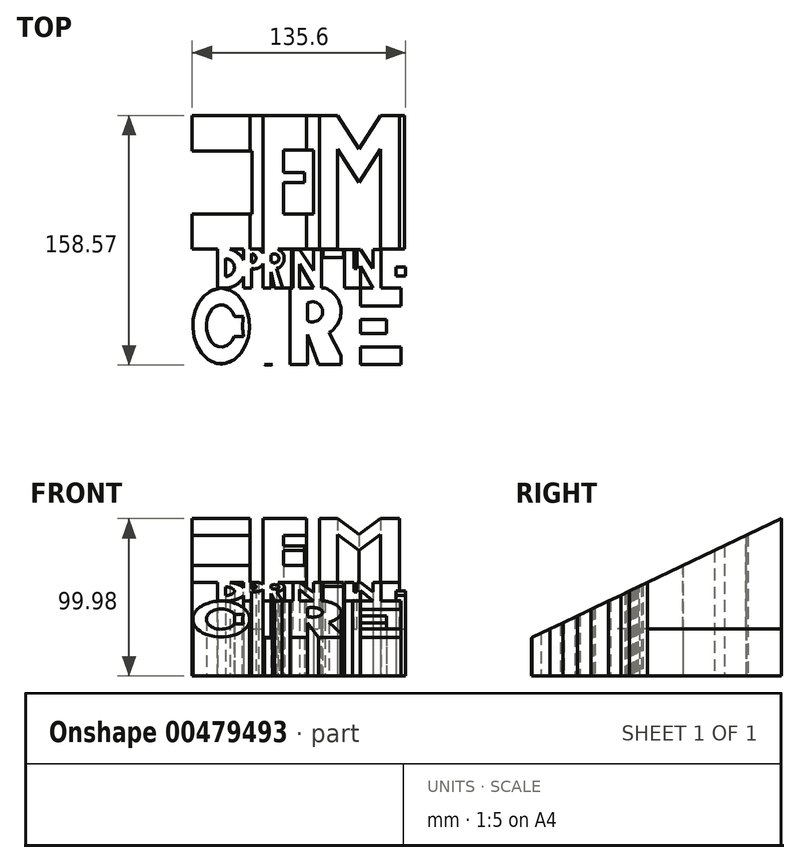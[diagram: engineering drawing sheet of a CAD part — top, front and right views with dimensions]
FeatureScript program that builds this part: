
annotation { "Feature Type Name" : "Feature", "Feature Type Description" : "" }
export const myFeature = defineFeature(function(context is Context, id is Id, definition is map)
    precondition{}
    {
        {
            var Q0;
            Q0=qCreatedBy(makeId("Top.planeOp"),FACE);
            var sketch = newSketch(context, id + "F0", { "sketchPlane" : qUnion([Q0])});
            skLineSegment(sketch, "E0.bottom", {"start": v(-89.26, 70.35) * mm, "end": v(-51.16, 70.35) * mm});
            skLineSegment(sketch, "E0.top", {"start": v(-89.26, 47.87) * mm, "end": v(-51.16, 47.87) * mm});
            skLineSegment(sketch, "E0.left", {"start": v(-89.26, 70.35) * mm, "end": v(-89.26, 47.87) * mm});
            skLineSegment(sketch, "E0.right", {"start": v(-51.16, 70.35) * mm, "end": v(-51.16, 47.87) * mm});
            skLineSegment(sketch, "E1.bottom", {"start": v(-89.26, 7.86) * mm, "end": v(-51.16, 7.86) * mm});
            skLineSegment(sketch, "E1.top", {"start": v(-89.26, -14.63) * mm, "end": v(-51.16, -14.63) * mm});
            skLineSegment(sketch, "E1.left", {"start": v(-89.26, 7.86) * mm, "end": v(-89.26, -14.63) * mm});
            skLineSegment(sketch, "E1.right", {"start": v(-51.16, 7.86) * mm, "end": v(-51.16, -14.63) * mm});
            skLineSegment(sketch, "E2.bottom", {"start": v(-76.85, 47.87) * mm, "end": v(-63.83, 47.87) * mm});
            skLineSegment(sketch, "E2.top", {"start": v(-76.85, 7.86) * mm, "end": v(-63.83, 7.86) * mm});
            skLineSegment(sketch, "E2.left", {"start": v(-76.85, 47.87) * mm, "end": v(-76.85, 7.86) * mm});
            skLineSegment(sketch, "E2.right", {"start": v(-63.83, 47.87) * mm, "end": v(-63.83, 7.86) * mm});
            skLineSegment(sketch, "E3.bottom", {"start": v(-51.16, 70.35) * mm, "end": v(-31.34, 70.35) * mm});
            skLineSegment(sketch, "E3.top", {"start": v(-51.16, -14.63) * mm, "end": v(-31.34, -14.63) * mm});
            skLineSegment(sketch, "E3.left", {"start": v(-51.16, 70.35) * mm, "end": v(-51.16, -14.63) * mm});
            skLineSegment(sketch, "E3.right", {"start": v(-31.34, 70.35) * mm, "end": v(-31.34, -14.63) * mm});
            skLineSegment(sketch, "E4.bottom", {"start": v(-31.34, 70.35) * mm, "end": v(-12.3, 70.35) * mm});
            skLineSegment(sketch, "E4.top", {"start": v(-31.34, 48.25) * mm, "end": v(-12.3, 48.25) * mm});
            skLineSegment(sketch, "E4.left", {"start": v(-31.34, 70.35) * mm, "end": v(-31.34, 48.25) * mm});
            skLineSegment(sketch, "E4.right", {"start": v(-12.3, 70.35) * mm, "end": v(-12.3, 48.25) * mm});
            skLineSegment(sketch, "E5.bottom", {"start": v(-31.34, -14.63) * mm, "end": v(-12.3, -14.63) * mm});
            skLineSegment(sketch, "E5.top", {"start": v(-31.34, 7.86) * mm, "end": v(-12.3, 7.86) * mm});
            skLineSegment(sketch, "E5.left", {"start": v(-31.34, -14.63) * mm, "end": v(-31.34, 7.86) * mm});
            skLineSegment(sketch, "E5.right", {"start": v(-12.3, -14.63) * mm, "end": v(-12.3, 7.86) * mm});
            skLineSegment(sketch, "E6.bottom", {"start": v(-31.34, 27.86) * mm, "end": v(-17.78, 27.86) * mm});
            skLineSegment(sketch, "E6.top", {"start": v(-31.34, 34.13) * mm, "end": v(-17.78, 34.13) * mm});
            skLineSegment(sketch, "E6.left", {"start": v(-31.34, 34.13) * mm, "end": v(-31.34, 27.86) * mm});
            skLineSegment(sketch, "E6.right", {"start": v(-17.78, 34.13) * mm, "end": v(-17.78, 27.86) * mm});
            skLineSegment(sketch, "E7.bottom", {"start": v(-12.3, 70.35) * mm, "end": v(2.95, 70.35) * mm});
            skLineSegment(sketch, "E7.top", {"start": v(-12.3, -14.63) * mm, "end": v(2.95, -14.63) * mm});
            skLineSegment(sketch, "E7.left", {"start": v(-12.3, 70.35) * mm, "end": v(-12.3, -14.63) * mm});
            skLineSegment(sketch, "E7.right", {"start": v(2.95, 70.35) * mm, "end": v(2.95, -14.63) * mm});
            skLineSegment(sketch, "E8.bottom", {"start": v(30.35, 70.35) * mm, "end": v(45.59, 70.35) * mm});
            skLineSegment(sketch, "E8.top", {"start": v(30.35, -14.63) * mm, "end": v(45.59, -14.63) * mm});
            skLineSegment(sketch, "E8.left", {"start": v(30.35, 70.35) * mm, "end": v(30.35, -14.63) * mm});
            skLineSegment(sketch, "E8.right", {"start": v(45.59, 70.35) * mm, "end": v(45.59, -14.63) * mm});
            skLineSegment(sketch, "E9", {"start": v(2.95, 70.35) * mm, "end": v(16.65, 49.1) * mm});
            skLineSegment(sketch, "E10", {"start": v(16.65, 49.1) * mm, "end": v(30.35, 70.35) * mm});
            skLineSegment(sketch, "E11", {"start": v(2.95, 49.1) * mm, "end": v(16.65, 27.86) * mm});
            skPoint(sketch, "E11.endSnap0", {"position": v(2.95, 27.86) * mm});
            skLineSegment(sketch, "E12", {"start": v(16.65, 27.86) * mm, "end": v(30.35, 49.1) * mm});
            skLineSegment(sketch, "E13.bottom", {"start": v(-63.83, 47.87) * mm, "end": v(-51.16, 47.87) * mm});
            skLineSegment(sketch, "E13.top", {"start": v(-63.83, 7.86) * mm, "end": v(-51.16, 7.86) * mm});
            skLineSegment(sketch, "E13.right", {"start": v(-51.16, 47.87) * mm, "end": v(-51.16, 7.86) * mm});
            skSolve(sketch);
        }
        {
            var Q0;
            Q0=qCreatedBy(makeId("Top.planeOp"),FACE);
            var sketch = newSketch(context, id + "F1", { "sketchPlane" : qUnion([Q0])});
            skLineSegment(sketch, "E14.bottom", {"start": v(-73.03, -14.35) * mm, "end": v(-67.95, -14.35) * mm});
            skLineSegment(sketch, "E14.top", {"start": v(-73.03, -39.24) * mm, "end": v(-67.95, -39.24) * mm});
            skLineSegment(sketch, "E14.left", {"start": v(-73.03, -14.35) * mm, "end": v(-73.03, -39.24) * mm});
            skLineSegment(sketch, "E14.right", {"start": v(-67.95, -14.35) * mm, "end": v(-67.95, -39.24) * mm});
            skArc(sketch, "E15", {"start": v(-67.95, -39.24) * mm, "mid": v(-55.5, -26.8) * mm, "end": v(-67.95, -14.35) * mm});
            skArc(sketch, "E16", {"start": v(-67.95, -31.89) * mm, "mid": v(-62.43, -26.25) * mm, "end": v(-67.95, -20.61) * mm});
            skLineSegment(sketch, "E17.bottom", {"start": v(-56.65, -14.35) * mm, "end": v(-51.57, -14.35) * mm});
            skLineSegment(sketch, "E17.top", {"start": v(-56.65, -39.24) * mm, "end": v(-51.57, -39.24) * mm});
            skLineSegment(sketch, "E17.left", {"start": v(-56.65, -14.35) * mm, "end": v(-56.65, -39.24) * mm});
            skLineSegment(sketch, "E17.right", {"start": v(-51.57, -14.35) * mm, "end": v(-51.57, -39.24) * mm});
            skArc(sketch, "E18", {"start": v(-51.57, -26.8) * mm, "mid": v(-43.27, -20.57) * mm, "end": v(-51.57, -14.35) * mm});
            skLineSegment(sketch, "E19", {"start": v(-51.57, -18.35) * mm, "end": v(-51.57, -18.35) * mm});
            skLineSegment(sketch, "E20.bottom", {"start": v(-44.12, -14.35) * mm, "end": v(-39.04, -14.35) * mm});
            skLineSegment(sketch, "E20.top", {"start": v(-44.12, -39.24) * mm, "end": v(-39.04, -39.24) * mm});
            skLineSegment(sketch, "E20.left", {"start": v(-44.12, -14.35) * mm, "end": v(-44.12, -39.24) * mm});
            skLineSegment(sketch, "E20.right", {"start": v(-39.04, -14.35) * mm, "end": v(-39.04, -39.24) * mm});
            skArc(sketch, "E21", {"start": v(-39.04, -26.8) * mm, "mid": v(-30.74, -20.57) * mm, "end": v(-39.04, -14.35) * mm});
            skArc(sketch, "E22", {"start": v(-39.04, -22.42) * mm, "mid": v(-34.12, -20.4) * mm, "end": v(-39.04, -18.4) * mm});
            skLineSegment(sketch, "E23", {"start": v(-31.86, -39.24) * mm, "end": v(-36.94, -39.24) * mm});
            skLineSegment(sketch, "E24", {"start": v(-31.86, -39.24) * mm, "end": v(-35.76, -26.89) * mm});
            skLineSegment(sketch, "E25", {"start": v(-39.04, -29) * mm, "end": v(-36.94, -39.24) * mm});
            skPoint(sketch, "E26.firstSnap0", {"position": v(-30.74, -20.57) * mm});
            skLineSegment(sketch, "E26.right", {"start": v(-26.11, -14.77) * mm, "end": v(-26.11, -39.24) * mm});
            skLineSegment(sketch, "E27.bottom", {"start": v(-26.11, -14.77) * mm, "end": v(-21.03, -14.77) * mm});
            skLineSegment(sketch, "E27.top", {"start": v(-26.11, -39.38) * mm, "end": v(-21.03, -39.38) * mm});
            skLineSegment(sketch, "E27.left", {"start": v(-26.11, -14.77) * mm, "end": v(-26.11, -39.38) * mm});
            skLineSegment(sketch, "E27.right", {"start": v(-21.03, -14.77) * mm, "end": v(-21.03, -39.38) * mm});
            skLineSegment(sketch, "E28", {"start": v(-21.03, -14.77) * mm, "end": v(-12.2, -28.04) * mm});
            skLineSegment(sketch, "E29", {"start": v(-12.2, -28.04) * mm, "end": v(-12.2, -14.77) * mm});
            skLineSegment(sketch, "E30", {"start": v(-21.03, -24.1) * mm, "end": v(-12.2, -39.38) * mm});
            skLineSegment(sketch, "E31", {"start": v(-12.2, -39.38) * mm, "end": v(-7.11, -39.38) * mm});
            skLineSegment(sketch, "E32", {"start": v(-7.11, -39.38) * mm, "end": v(-7.11, -14.77) * mm});
            skLineSegment(sketch, "E33", {"start": v(-7.11, -14.77) * mm, "end": v(-12.2, -14.77) * mm});
            skLineSegment(sketch, "E34.bottom", {"start": v(-7.11, -14.77) * mm, "end": v(7.49, -14.77) * mm});
            skLineSegment(sketch, "E34.top", {"start": v(-7.11, -19.85) * mm, "end": v(7.49, -19.85) * mm});
            skLineSegment(sketch, "E34.left", {"start": v(-7.11, -14.77) * mm, "end": v(-7.11, -19.85) * mm});
            skLineSegment(sketch, "E34.right", {"start": v(7.49, -14.77) * mm, "end": v(7.49, -19.85) * mm});
            skLineSegment(sketch, "E35.bottom", {"start": v(-2.26, -19.85) * mm, "end": v(2.82, -19.85) * mm});
            skLineSegment(sketch, "E35.top", {"start": v(-2.26, -39.24) * mm, "end": v(2.82, -39.24) * mm});
            skLineSegment(sketch, "E35.left", {"start": v(-2.26, -19.85) * mm, "end": v(-2.26, -39.24) * mm});
            skLineSegment(sketch, "E35.right", {"start": v(2.82, -19.85) * mm, "end": v(2.82, -39.24) * mm});
            skPoint(sketch, "E36.firstSnap0", {"position": v(7.49, -16.42) * mm});
            skLineSegment(sketch, "E36.bottom", {"start": v(7.49, -14.77) * mm, "end": v(12.57, -14.77) * mm});
            skLineSegment(sketch, "E36.top", {"start": v(7.49, -39.18) * mm, "end": v(12.57, -39.18) * mm});
            skLineSegment(sketch, "E36.left", {"start": v(7.49, -14.77) * mm, "end": v(7.49, -39.18) * mm});
            skLineSegment(sketch, "E36.right", {"start": v(12.57, -14.77) * mm, "end": v(12.57, -39.18) * mm});
            skLineSegment(sketch, "E37.bottom", {"start": v(12.57, -14.77) * mm, "end": v(17.65, -14.77) * mm});
            skLineSegment(sketch, "E37.top", {"start": v(12.57, -39.38) * mm, "end": v(17.65, -39.38) * mm});
            skLineSegment(sketch, "E37.left", {"start": v(12.57, -14.77) * mm, "end": v(12.57, -39.38) * mm});
            skLineSegment(sketch, "E37.right", {"start": v(17.65, -14.77) * mm, "end": v(17.65, -39.38) * mm});
            skLineSegment(sketch, "E38", {"start": v(17.65, -14.77) * mm, "end": v(25.58, -26.99) * mm});
            skLineSegment(sketch, "E39", {"start": v(25.58, -26.99) * mm, "end": v(25.58, -14.77) * mm});
            skLineSegment(sketch, "E40", {"start": v(17.65, -25.15) * mm, "end": v(25.58, -39.38) * mm});
            skLineSegment(sketch, "E41", {"start": v(25.58, -39.38) * mm, "end": v(30.66, -39.38) * mm});
            skLineSegment(sketch, "E42", {"start": v(30.66, -39.38) * mm, "end": v(30.66, -14.77) * mm});
            skLineSegment(sketch, "E43", {"start": v(30.66, -14.77) * mm, "end": v(25.58, -14.77) * mm});
            skLineSegment(sketch, "E44.bottom", {"start": v(40.35, -25.97) * mm, "end": v(46.34, -25.97) * mm});
            skLineSegment(sketch, "E44.top", {"start": v(40.35, -31.54) * mm, "end": v(46.34, -31.54) * mm});
            skLineSegment(sketch, "E44.left", {"start": v(40.35, -25.97) * mm, "end": v(40.35, -31.54) * mm});
            skLineSegment(sketch, "E44.right", {"start": v(46.34, -25.97) * mm, "end": v(46.34, -31.54) * mm});
            skArc(sketch, "E45", {"start": v(46.3, -22.16) * mm, "mid": v(37.94, -14.8) * mm, "end": v(30.66, -23.22) * mm});
            skArc(sketch, "E46", {"start": v(30.66, -31.54) * mm, "mid": v(38.5, -39.38) * mm, "end": v(46.34, -31.54) * mm});
            skLineSegment(sketch, "E47", {"start": v(46.3, -22.16) * mm, "end": v(40.35, -22.16) * mm});
            skArc(sketch, "E48", {"start": v(40.35, -22.16) * mm, "mid": v(38.47, -20.68) * mm, "end": v(36.6, -22.16) * mm});
            skPoint(sketch, "E49.startSnap0", {"position": v(43.34, -31.54) * mm});
            skLineSegment(sketch, "E50", {"start": v(36.6, -22.16) * mm, "end": v(36.6, -31.68) * mm});
            skArc(sketch, "E51", {"start": v(36.6, -31.68) * mm, "mid": v(40.05, -35.06) * mm, "end": v(43.35, -31.54) * mm});
            skLineSegment(sketch, "E52", {"start": v(30.66, -39.38) * mm, "end": v(38.06, -39.38) * mm});
            skPoint(sketch, "E52.endSnap0", {"position": v(38.5, -39.38) * mm});
            skLineSegment(sketch, "E53", {"start": v(30.66, -14.77) * mm, "end": v(38.47, -14.77) * mm});
            skPoint(sketch, "E53.endSnap0", {"position": v(38.47, -20.68) * mm});
            skArc(sketch, "E54", {"start": v(-51.57, -23.17) * mm, "mid": v(-48.95, -20.31) * mm, "end": v(-51.57, -17.45) * mm});
            skArc(sketch, "E55", {"start": v(-67.95, -31.89) * mm, "mid": v(-62.45, -26.25) * mm, "end": v(-67.95, -20.61) * mm});
            skLineSegment(sketch, "E56", {"start": v(-67.95, -20.61) * mm, "end": v(-67.95, -31.89) * mm});
            skArc(sketch, "E57", {"start": v(-51.57, -23.17) * mm, "mid": v(-48.71, -20.31) * mm, "end": v(-51.57, -17.45) * mm});
            skLineSegment(sketch, "E58", {"start": v(-51.57, -17.45) * mm, "end": v(-51.57, -23.17) * mm});
            skArc(sketch, "E59", {"start": v(-39.04, -22.42) * mm, "mid": v(-34.75, -20.4) * mm, "end": v(-39.04, -18.4) * mm});
            skLineSegment(sketch, "E60", {"start": v(-35.76, -26.89) * mm, "end": v(-31.86, -39.24) * mm});
            skLineSegment(sketch, "E61", {"start": v(-67.95, -39.24) * mm, "end": v(-56.65, -39.24) * mm});
            skLineSegment(sketch, "E62", {"start": v(-51.57, -39.24) * mm, "end": v(-44.12, -39.24) * mm});
            skLineSegment(sketch, "E63", {"start": v(-21.03, -39.38) * mm, "end": v(-12.2, -39.38) * mm});
            skLineSegment(sketch, "E64", {"start": v(2.82, -39.24) * mm, "end": v(7.49, -39.18) * mm});
            skLineSegment(sketch, "E65", {"start": v(17.65, -39.38) * mm, "end": v(25.58, -39.38) * mm});
            skLineSegment(sketch, "E66", {"start": v(-39.04, -39.24) * mm, "end": v(-26.11, -39.24) * mm});
            skLineSegment(sketch, "E67.bottom", {"start": v(-32.23, -14.22) * mm, "end": v(-23.57, -14.22) * mm});
            skLineSegment(sketch, "E67.top", {"start": v(-32.23, -39.38) * mm, "end": v(-23.57, -39.38) * mm});
            skLineSegment(sketch, "E67.left", {"start": v(-32.23, -14.22) * mm, "end": v(-32.23, -39.38) * mm});
            skLineSegment(sketch, "E67.right", {"start": v(-23.57, -14.22) * mm, "end": v(-23.57, -39.38) * mm});
            skSolve(sketch);
        }
        {
            var Q0;
            Q0=qCreatedBy(makeId("Top.planeOp"),FACE);
            var sketch = newSketch(context, id + "F2", { "sketchPlane" : qUnion([Q0])});
            skLineSegment(sketch, "E68", {"start": v(-89.42, -14.56) * mm, "end": v(-81.13, -14.56) * mm});
            skLineSegment(sketch, "E69", {"start": v(-81.13, -14.56) * mm, "end": v(-72.84, -14.56) * mm});
            skArc(sketch, "E70", {"start": v(-72.59, -21.07) * mm, "mid": v(-81.1, -14.56) * mm, "end": v(-89.7, -20.95) * mm});
            skArc(sketch, "E71", {"start": v(-89.98, -30.4) * mm, "mid": v(-81.43, -38.22) * mm, "end": v(-72.38, -30.99) * mm});
            skLineSegment(sketch, "E72", {"start": v(-89.7, -20.95) * mm, "end": v(-86.13, -20.95) * mm});
            skLineSegment(sketch, "E73", {"start": v(-89.98, -30.4) * mm, "end": v(-86.13, -30.4) * mm});
            skLineSegment(sketch, "E74", {"start": v(-81.16, -24.23) * mm, "end": v(-81.16, -27.8) * mm});
            skArc(sketch, "E75", {"start": v(-81.16, -24.23) * mm, "mid": v(-80.8, -18.3) * mm, "end": v(-86.13, -20.95) * mm});
            skArc(sketch, "E76", {"start": v(-86.13, -30.4) * mm, "mid": v(-80.7, -34.74) * mm, "end": v(-81.16, -27.8) * mm});
            skArc(sketch, "E77", {"start": v(-77.53, -26.18) * mm, "mid": v(-74.4, -24.26) * mm, "end": v(-72.59, -21.07) * mm});
            skArc(sketch, "E78", {"start": v(-72.38, -30.99) * mm, "mid": v(-74.34, -27.92) * mm, "end": v(-77.53, -26.18) * mm});
            skPoint(sketch, "E79.endSnap0", {"position": v(-81.43, -38.22) * mm});
            skSolve(sketch);
        }
        {
            var Q0;
            Q0=qCreatedBy(makeId("Top.planeOp"),FACE);
            var sketch = newSketch(context, id + "F3", { "sketchPlane" : qUnion([Q0])});
            skLineSegment(sketch, "E80.bottom", {"start": v(-27.05, -39.34) * mm, "end": v(-16.01, -39.34) * mm});
            skLineSegment(sketch, "E80.top", {"start": v(-27.05, -87.9) * mm, "end": v(-16.01, -87.9) * mm});
            skLineSegment(sketch, "E80.left", {"start": v(-27.05, -39.34) * mm, "end": v(-27.05, -87.9) * mm});
            skLineSegment(sketch, "E80.right", {"start": v(-16.01, -39.34) * mm, "end": v(-16.01, -87.9) * mm});
            skLineSegment(sketch, "E81", {"start": v(-2.07, -87.9) * mm, "end": v(9.8, -87.9) * mm});
            skLineSegment(sketch, "E82.bottom", {"start": v(5.15, -39.34) * mm, "end": v(17.67, -39.34) * mm});
            skLineSegment(sketch, "E82.top", {"start": v(5.15, -87.9) * mm, "end": v(17.67, -87.9) * mm});
            skLineSegment(sketch, "E82.left", {"start": v(5.15, -39.34) * mm, "end": v(5.15, -87.9) * mm});
            skLineSegment(sketch, "E82.right", {"start": v(17.67, -39.34) * mm, "end": v(17.67, -87.9) * mm});
            skLineSegment(sketch, "E83.bottom", {"start": v(17.67, -39.34) * mm, "end": v(43.46, -39.34) * mm});
            skLineSegment(sketch, "E83.top", {"start": v(17.67, -50.64) * mm, "end": v(43.46, -50.64) * mm});
            skLineSegment(sketch, "E83.left", {"start": v(17.67, -39.34) * mm, "end": v(17.67, -50.64) * mm});
            skLineSegment(sketch, "E83.right", {"start": v(43.46, -39.34) * mm, "end": v(43.46, -50.64) * mm});
            skLineSegment(sketch, "E84.bottom", {"start": v(17.67, -87.9) * mm, "end": v(43.46, -87.9) * mm});
            skLineSegment(sketch, "E84.top", {"start": v(17.67, -76.6) * mm, "end": v(43.46, -76.6) * mm});
            skLineSegment(sketch, "E84.left", {"start": v(17.67, -87.9) * mm, "end": v(17.67, -76.6) * mm});
            skLineSegment(sketch, "E84.right", {"start": v(43.46, -87.9) * mm, "end": v(43.46, -76.6) * mm});
            skLineSegment(sketch, "E85.bottom", {"start": v(17.67, -59.12) * mm, "end": v(34.28, -59.12) * mm});
            skLineSegment(sketch, "E85.top", {"start": v(17.67, -68.25) * mm, "end": v(34.28, -68.25) * mm});
            skLineSegment(sketch, "E85.left", {"start": v(17.67, -59.12) * mm, "end": v(17.67, -68.25) * mm});
            skLineSegment(sketch, "E85.right", {"start": v(34.28, -59.12) * mm, "end": v(34.28, -68.25) * mm});
            skPoint(sketch, "E86.endSnap0", {"position": v(-72.4, -92.39) * mm});
            skLineSegment(sketch, "E87", {"start": v(-48.63, -87.9) * mm, "end": v(-27.05, -87.9) * mm});
            skLineSegment(sketch, "E88", {"start": v(-2.07, -87.9) * mm, "end": v(43.46, -87.9) * mm});
            skLineSegment(sketch, "E89", {"start": v(-16.01, -39.34) * mm, "end": v(29.75, -39.34) * mm});
            skLineSegment(sketch, "E90", {"start": v(-27.05, -39.34) * mm, "end": v(-14.53, -39.34) * mm});
            skLineSegment(sketch, "E91", {"start": v(-16.01, -87.9) * mm, "end": v(-2.07, -87.9) * mm});
            skLineSegment(sketch, "E92", {"start": v(-72.57, -87.9) * mm, "end": v(-48.63, -87.9) * mm});
            skPoint(sketch, "E93.startSnap0", {"position": v(-61.69, -59.33) * mm});
            skLineSegment(sketch, "E94", {"start": v(-16.01, -68.75) * mm, "end": v(-9.04, -87.9) * mm});
            skArc(sketch, "E95", {"start": v(-16.01, -68.75) * mm, "mid": v(5.37, -54.04) * mm, "end": v(-16.01, -39.34) * mm});
            skArc(sketch, "E96", {"start": v(-16.01, -59.96) * mm, "mid": v(-6.33, -54.38) * mm, "end": v(-16.01, -48.8) * mm});
            skLineSegment(sketch, "E97", {"start": v(-2.39, -67.61) * mm, "end": v(8.1, -87.9) * mm});
            skEllipse(sketch, "E98", {"center": v(-40.83, -63.37) * mm, "majorRadius": 24.85 * mm, "minorRadius": 16.36 * mm, "majorAxis": v(0, 1)});
            skEllipse(sketch, "E99", {"center": v(-40.83, -63.37) * mm, "majorRadius": 11.51 * mm, "minorRadius": 6.34 * mm, "majorAxis": v(0, 1)});
            skEllipse(sketch, "E100", {"center": v(-70.8, -63.37) * mm, "majorRadius": 24 * mm, "minorRadius": 18.03 * mm, "majorAxis": v(0, 1)});
            skEllipse(sketch, "E101", {"center": v(-70.8, -63.37) * mm, "majorRadius": 13.42 * mm, "minorRadius": 9.43 * mm, "majorAxis": v(0, 1)});
            skLineSegment(sketch, "E102", {"start": v(-62.36, -57.4) * mm, "end": v(-53.34, -57.4) * mm});
            skLineSegment(sketch, "E103", {"start": v(-62.59, -69.96) * mm, "end": v(-53.47, -69.96) * mm});
            skSolve(sketch);
        }
        {
            var Q0;
            Q0=makeQuery(id+"F3.imprint","IMPRINT",FACE,{"disambiguationData":[TD([[makeQuery(id+"F3.imprint","IMPRINT",EDGE,{"derivedFrom":sQuery(id+"F3.wireOp",EDGE,"E93")}),-1.0]])]});
            var Q1;
            {var subQ0=sQuery(id+"F3.wireOp",EDGE,"GElmIXpN-kcJR-45oa-h3sK-QHrJCuWuAJcQ");var subQ1=sQuery(id+"F3.wireOp",EDGE,"etVh0nDV-C5XI-KxPU-PWaB-zNqrgVtYXJuy");var subQ3=makeQuery(id+"F3.imprint","INTERSECT",VERTEX,{"derivedFrom":[subQ1,subQ0]});Q1=makeQuery(id+"F3.imprint","IMPRINT",FACE,{"disambiguationData":[TD([[makeQuery(id+"F3.imprint","IMPRINT",EDGE,{"disambiguationData":[TD([[subQ3,-1.0]])],"derivedFrom":subQ1}),1.0]])]});}
            var Q2;
            Q2=makeQuery(id+"F3.imprint","IMPRINT",FACE,{"disambiguationData":[TD([[makeQuery(id+"F3.imprint","IMPRINT",EDGE,{"derivedFrom":sQuery(id+"F3.wireOp",EDGE,"l2BAxcx8-wpF1-YFFp-7Sex-uG9L4fK84GIy")}),1.0]])]});
            var Q3;
            Q3=makeQuery(id+"F3.imprint","IMPRINT",FACE,{"disambiguationData":[TD([[makeQuery(id+"F3.imprint","IMPRINT",EDGE,{"derivedFrom":sQuery(id+"F3.wireOp",EDGE,"Tai5gYko-rnaj-8Qc9-2tER-s00ccv3sg9T1")}),-1.0]])]});
            var Q4;
            {var subQ0=sQuery(id+"F3.wireOp",EDGE,"etVh0nDV-C5XI-KxPU-PWaB-zNqrgVtYXJuy");var subQ1=sQuery(id+"F3.wireOp",EDGE,"E80.left");var subQ3=makeQuery(id+"F3.imprint","INTERSECT",VERTEX,{"derivedFrom":[subQ1,subQ0]});Q4=makeQuery(id+"F3.imprint","IMPRINT",FACE,{"disambiguationData":[TD([[makeQuery(id+"F3.imprint","IMPRINT",EDGE,{"disambiguationData":[TD([[subQ3,-1.0]])],"derivedFrom":subQ1}),1.0]])]});}
            var Q5;
            {var subQ7=sQuery(id+"F3.wireOp",EDGE,"E80.bottom");Q5=makeQuery(id+"F3.imprint","IMPRINT",FACE,{"disambiguationData":[TD([[makeQuery(id+"F3.imprint","IMPRINT",EDGE,{"derivedFrom":subQ7}),-1.0]])]});}
            var Q6;
            {var subQ0=sQuery(id+"F3.wireOp",EDGE,"9Uwg85qv-AG06-xsUL-vuyy-mQr5ySh0xjGx");var subQ1=sQuery(id+"F3.wireOp",EDGE,"E87");var subQ3=makeQuery(id+"F3.imprint","INTERSECT",VERTEX,{"derivedFrom":[subQ1,subQ0]});Q6=makeQuery(id+"F3.imprint","IMPRINT",FACE,{"disambiguationData":[TD([[makeQuery(id+"F3.imprint","IMPRINT",EDGE,{"disambiguationData":[TD([[subQ3,1.0]])],"derivedFrom":subQ1}),-1.0]])]});}
            var Q7;
            {var subQ0=sQuery(id+"F3.wireOp",EDGE,"9Uwg85qv-AG06-xsUL-vuyy-mQr5ySh0xjGx");var subQ1=sQuery(id+"F3.wireOp",EDGE,"E80.left");var subQ3=makeQuery(id+"F3.imprint","INTERSECT",VERTEX,{"derivedFrom":[subQ1,subQ0]});Q7=makeQuery(id+"F3.imprint","IMPRINT",FACE,{"disambiguationData":[TD([[makeQuery(id+"F3.imprint","IMPRINT",EDGE,{"disambiguationData":[TD([[subQ3,1.0]])],"derivedFrom":subQ1}),1.0]])]});}
            var Q8;
            {var subQ0=sQuery(id+"F3.wireOp",EDGE,"goEZywdV-8XkG-8Sym-g4On-3OGV7yo023wS");var subQ1=sQuery(id+"F3.wireOp",EDGE,"9Uwg85qv-AG06-xsUL-vuyy-mQr5ySh0xjGx");var subQ3=makeQuery(id+"F3.imprint","INTERSECT",VERTEX,{"derivedFrom":[subQ1,subQ0]});Q8=makeQuery(id+"F3.imprint","IMPRINT",FACE,{"disambiguationData":[TD([[makeQuery(id+"F3.imprint","IMPRINT",EDGE,{"disambiguationData":[TD([[subQ3,1.0]])],"derivedFrom":subQ1}),1.0]])]});}
            var Q9;
            {var subQ10=sQuery(id+"F3.wireOp",EDGE,"vgvU5bvX-y910-j5x7-Pnl7-edi9nkagyyvk");Q9=makeQuery(id+"F3.imprint","IMPRINT",FACE,{"disambiguationData":[TD([[makeQuery(id+"F3.imprint","IMPRINT",EDGE,{"derivedFrom":subQ10}),1.0]])]});}
            var Q10;
            {var subQ9=sQuery(id+"F3.wireOp",EDGE,"ZULs1xFT-bYxo-X5Mw-NcRk-gdkzuhtu9iQL");Q10=makeQuery(id+"F3.imprint","IMPRINT",FACE,{"disambiguationData":[TD([[makeQuery(id+"F3.imprint","IMPRINT",EDGE,{"derivedFrom":subQ9}),-1.0]])]});}
            var Q11;
            {var subQ0=sQuery(id+"F3.wireOp",EDGE,"UGmMbKpx-ic0C-BP45-GIFm-G44WuJZ7rcJZ");var subQ1=sQuery(id+"F3.wireOp",EDGE,"E82.left");var subQ2=makeQuery(id+"F3.imprint","INTERSECT",VERTEX,{"disambiguationData":[OD(0.0)],"derivedFrom":[subQ1,subQ0]});Q11=makeQuery(id+"F3.imprint","IMPRINT",FACE,{"disambiguationData":[TD([[makeQuery(id+"F3.imprint","IMPRINT",EDGE,{"disambiguationData":[TD([[subQ2,-1.0]])],"derivedFrom":subQ1}),1.0]])]});}
            var Q12;
            {var subQ5=sQuery(id+"F3.wireOp",EDGE,"5uwGIrsL-Ax3l-KrJ3-TsMS-mPTyOWhAeuEh");Q12=makeQuery(id+"F3.imprint","IMPRINT",FACE,{"disambiguationData":[TD([[makeQuery(id+"F3.imprint","IMPRINT",EDGE,{"derivedFrom":subQ5}),1.0]])]});}
            var Q13;
            {var subQ0=sQuery(id+"F3.wireOp",EDGE,"E88");var subQ1=sQuery(id+"F3.wireOp",EDGE,"QoJ9POKL-7dSj-Kbwg-M42Z-KDTpscI53ORy");var subQ2=makeQuery(id+"F3.imprint","INTERSECT",VERTEX,{"derivedFrom":[subQ1,subQ0]});Q13=makeQuery(id+"F3.imprint","IMPRINT",FACE,{"disambiguationData":[TD([[makeQuery(id+"F3.imprint","IMPRINT",EDGE,{"disambiguationData":[TD([[subQ2,1.0]])],"derivedFrom":subQ1}),-1.0]])]});}
            var Q14;
            {var subQ3=sQuery(id+"F3.wireOp",EDGE,"E83.left");Q14=makeQuery(id+"F3.imprint","IMPRINT",FACE,{"disambiguationData":[TD([[makeQuery(id+"F3.imprint","IMPRINT",EDGE,{"derivedFrom":subQ3}),-1.0]])]});}
            var Q15;
            Q15=makeQuery(id+"F3.imprint","IMPRINT",FACE,{"disambiguationData":[TD([[makeQuery(id+"F3.imprint","IMPRINT",EDGE,{"derivedFrom":sQuery(id+"F3.wireOp",EDGE,"E84.top")}),-1.0]])]});
            var Q16;
            Q16=makeQuery(id+"F3.imprint","IMPRINT",FACE,{"disambiguationData":[TD([[makeQuery(id+"F3.imprint","IMPRINT",EDGE,{"derivedFrom":sQuery(id+"F3.wireOp",EDGE,"E85.bottom")}),-1.0]])]});
            var Q17;
            {var subQ1=sQuery(id+"F3.wireOp",EDGE,"E83.bottom");Q17=makeQuery(id+"F3.imprint","IMPRINT",FACE,{"disambiguationData":[TD([[makeQuery(id+"F3.imprint","IMPRINT",EDGE,{"derivedFrom":subQ1}),-1.0]])]});}
            var Q18;
            {var subQ5=sQuery(id+"F3.wireOp",EDGE,"E80.top");Q18=makeQuery(id+"F3.imprint","IMPRINT",FACE,{"disambiguationData":[TD([[makeQuery(id+"F3.imprint","IMPRINT",EDGE,{"derivedFrom":subQ5}),1.0]])]});}
            var Q19;
            {var subQ0=sQuery(id+"F3.wireOp",EDGE,"iaVYXmuH-C6zT-0Hll-rQQs-5zNDWjSzhZfG");var subQ1=sQuery(id+"F3.wireOp",EDGE,"E82.left");var subQ2=makeQuery(id+"F3.imprint","INTERSECT",VERTEX,{"disambiguationData":[OD(0.0)],"derivedFrom":[subQ1,subQ0]});Q19=makeQuery(id+"F3.imprint","IMPRINT",FACE,{"disambiguationData":[TD([[makeQuery(id+"F3.imprint","IMPRINT",EDGE,{"disambiguationData":[TD([[subQ2,-1.0]])],"derivedFrom":subQ1}),1.0]])]});}
            var Q20;
            {var subQ10=sQuery(id+"F3.wireOp",EDGE,"W87mtJ7x-wgiw-5JIF-yIz9-pi0v8XZ7OW02");Q20=makeQuery(id+"F3.imprint","IMPRINT",FACE,{"disambiguationData":[TD([[makeQuery(id+"F3.imprint","IMPRINT",EDGE,{"derivedFrom":subQ10}),-1.0]])]});}
            var Q21;
            {var subQ0=sQuery(id+"F3.wireOp",EDGE,"L14g0OWl-b5Mz-6KAP-ZlKC-kIkRNDyMzksr");var subQ1=sQuery(id+"F3.wireOp",EDGE,"E82.left");var subQ2=makeQuery(id+"F3.imprint","INTERSECT",VERTEX,{"disambiguationData":[OD(0.0)],"derivedFrom":[subQ1,subQ0]});Q21=makeQuery(id+"F3.imprint","IMPRINT",FACE,{"disambiguationData":[TD([[makeQuery(id+"F3.imprint","IMPRINT",EDGE,{"disambiguationData":[TD([[subQ2,-1.0]])],"derivedFrom":subQ1}),1.0]])]});}
            var Q22;
            {var subQ3=sQuery(id+"F3.wireOp",EDGE,"E96");Q22=makeQuery(id+"F3.imprint","IMPRINT",FACE,{"disambiguationData":[TD([[makeQuery(id+"F3.imprint","IMPRINT",EDGE,{"derivedFrom":subQ3}),-1.0]])]});}
            var Q23;
            {var subQ0=sQuery(id+"F3.wireOp",EDGE,"E94");Q23=makeQuery(id+"F3.imprint","IMPRINT",FACE,{"disambiguationData":[TD([[makeQuery(id+"F3.imprint","IMPRINT",EDGE,{"derivedFrom":subQ0}),1.0]])]});}
            var Q24;
            {var subQ0=sQuery(id+"F3.wireOp",EDGE,"E95");var subQ1=sQuery(id+"F3.wireOp",EDGE,"E82.left");var subQ2=makeQuery(id+"F3.imprint","INTERSECT",VERTEX,{"disambiguationData":[OD(0.0)],"derivedFrom":[subQ1,subQ0]});Q24=makeQuery(id+"F3.imprint","IMPRINT",FACE,{"disambiguationData":[TD([[makeQuery(id+"F3.imprint","IMPRINT",EDGE,{"disambiguationData":[TD([[subQ2,-1.0]])],"derivedFrom":subQ1}),1.0]])]});}
            var Q25;
            {var subQ0=sQuery(id+"F3.wireOp",EDGE,"E88");var subQ1=sQuery(id+"F3.wireOp",EDGE,"E82.left");var subQ2=makeQuery(id+"F3.imprint","INTERSECT",VERTEX,{"derivedFrom":[subQ1,subQ0]});Q25=makeQuery(id+"F3.imprint","IMPRINT",FACE,{"disambiguationData":[TD([[makeQuery(id+"F3.imprint","IMPRINT",EDGE,{"disambiguationData":[TD([[subQ2,1.0]])],"derivedFrom":subQ1}),1.0]])]});}
            var Q26;
            {var subQ0=sQuery(id+"F3.wireOp",EDGE,"dAoB9NSq-ERkH-hq60-yBYx-hBlx5KMwvAX0");Q26=makeQuery(id+"F3.imprint","IMPRINT",FACE,{"disambiguationData":[TD([[makeQuery(id+"F3.imprint","IMPRINT",EDGE,{"derivedFrom":subQ0}),-1.0]])]});}
            var Q27;
            Q27=makeQuery(id+"F3.imprint","IMPRINT",FACE,{"disambiguationData":[TD([[makeQuery(id+"F3.imprint","IMPRINT",EDGE,{"derivedFrom":sQuery(id+"F3.wireOp",EDGE,"E99")}),-1.0]])]});
            var Q28;
            {var subQ0=sQuery(id+"F3.wireOp",EDGE,"FfS5zIeq-Qh4c-nK4M-JezB-Kwh0gAgPYNTQ");var subQ1=sQuery(id+"F3.wireOp",EDGE,"E98");var subQ2=makeQuery(id+"F3.imprint","INTERSECT",VERTEX,{"disambiguationData":[OD(0.0)],"derivedFrom":[subQ1,subQ0]});Q28=makeQuery(id+"F3.imprint","IMPRINT",FACE,{"disambiguationData":[TD([[makeQuery(id+"F3.imprint","IMPRINT",EDGE,{"disambiguationData":[TD([[subQ2,1.0]])],"derivedFrom":subQ1}),1.0]])]});}
            var Q29;
            {var subQ0=sQuery(id+"F3.wireOp",EDGE,"XQu2pely-f4cg-mbWW-zxsq-JVxlkJcybIhI");Q29=makeQuery(id+"F3.imprint","IMPRINT",FACE,{"disambiguationData":[TD([[makeQuery(id+"F3.imprint","IMPRINT",EDGE,{"derivedFrom":subQ0}),1.0]])]});}
            var Q30;
            {var subQ5=sQuery(id+"F3.wireOp",EDGE,"E100");var subQ6=sQuery(id+"F3.wireOp",EDGE,"E98");var subQ10=makeQuery(id+"F3.imprint","INTERSECT",VERTEX,{"disambiguationData":[OD(0.0)],"derivedFrom":[subQ6,subQ5]});Q30=makeQuery(id+"F3.imprint","IMPRINT",FACE,{"disambiguationData":[TD([[makeQuery(id+"F3.imprint","IMPRINT",EDGE,{"disambiguationData":[TD([[subQ10,-1.0]])],"derivedFrom":subQ6}),-1.0]])]});}
            var Q31;
            {var subQ0=sQuery(id+"F3.wireOp",EDGE,"E100");var subQ1=sQuery(id+"F3.wireOp",EDGE,"E98");var subQ2=makeQuery(id+"F3.imprint","INTERSECT",VERTEX,{"disambiguationData":[OD(0.0)],"derivedFrom":[subQ1,subQ0]});Q31=makeQuery(id+"F3.imprint","IMPRINT",FACE,{"disambiguationData":[TD([[makeQuery(id+"F3.imprint","IMPRINT",EDGE,{"disambiguationData":[TD([[subQ2,-1.0]])],"derivedFrom":subQ1}),1.0]])]});}
            var Q32;
            {var subQ0=sQuery(id+"F3.wireOp",EDGE,"E100");var subQ1=sQuery(id+"F3.wireOp",EDGE,"E98");var subQ2=makeQuery(id+"F3.imprint","INTERSECT",VERTEX,{"disambiguationData":[OD(1.0)],"derivedFrom":[subQ1,subQ0]});Q32=makeQuery(id+"F3.imprint","IMPRINT",FACE,{"disambiguationData":[TD([[makeQuery(id+"F3.imprint","IMPRINT",EDGE,{"disambiguationData":[TD([[subQ2,1.0]])],"derivedFrom":subQ1}),1.0]])]});}
            var Q33;
            {var subQ0=sQuery(id+"F3.wireOp",EDGE,"E90");var subQ1=sQuery(id+"F3.wireOp",EDGE,"E89");var subQ2=makeQuery(id+"F3.imprint","INTERSECT",VERTEX,{"derivedFrom":[subQ1,subQ0]});Q33=makeQuery(id+"F3.imprint","IMPRINT",FACE,{"disambiguationData":[TD([[makeQuery(id+"F3.imprint","IMPRINT",EDGE,{"disambiguationData":[TD([[subQ2,-1.0]])],"derivedFrom":subQ1}),1.0]])]});}
            var Q34;
            {var subQ0=sQuery(id+"F3.wireOp",EDGE,"E98");var subQ1=sQuery(id+"F3.wireOp",EDGE,"E80.left");var subQ2=makeQuery(id+"F3.imprint","INTERSECT",VERTEX,{"disambiguationData":[OD(0.0)],"derivedFrom":[subQ1,subQ0]});Q34=makeQuery(id+"F3.imprint","IMPRINT",FACE,{"disambiguationData":[TD([[makeQuery(id+"F3.imprint","IMPRINT",EDGE,{"disambiguationData":[TD([[subQ2,-1.0]])],"derivedFrom":subQ1}),1.0]])]});}
            var Q35;
            {var subQ0=sQuery(id+"F3.wireOp",EDGE,"E102");var subQ1=sQuery(id+"F3.wireOp",EDGE,"E98");var subQ2=makeQuery(id+"F3.imprint","INTERSECT",VERTEX,{"derivedFrom":[subQ1,subQ0]});Q35=makeQuery(id+"F3.imprint","IMPRINT",FACE,{"disambiguationData":[TD([[makeQuery(id+"F3.imprint","IMPRINT",EDGE,{"disambiguationData":[TD([[subQ2,-1.0]])],"derivedFrom":subQ1}),1.0]])]});}
            extrude(context, id + "F4", {"entities" : qUnion([Q0, Q1, Q2, Q3, Q4, Q5, Q6, Q7, Q8, Q9, Q10, Q11, Q12, Q13, Q14, Q15, Q16, Q17, Q18, Q19, Q20, Q21, Q22, Q23, Q24, Q25, Q26, Q27, Q28, Q29, Q30, Q31, Q32, Q33, Q34, Q35]), "depth" : 100 * mm, "offsetDistance" : 25 * mm});
        }
        {
            var Q0;
            Q0=makeQuery(id+"F2.imprint","IMPRINT",FACE,{"disambiguationData":[TD([[makeQuery(id+"F2.imprint","IMPRINT",EDGE,{"derivedFrom":sQuery(id+"F2.wireOp",EDGE,"E71")}),1.0]])]});
            var Q1;
            {var subQ2=sQuery(id+"F1.wireOp",EDGE,"E14.bottom");Q1=makeQuery(id+"F1.imprint","IMPRINT",FACE,{"disambiguationData":[TD([[makeQuery(id+"F1.imprint","IMPRINT",EDGE,{"derivedFrom":subQ2}),-1.0]])]});}
            var Q2;
            {var subQ9=sQuery(id+"F1.wireOp",EDGE,"E16");Q2=makeQuery(id+"F1.imprint","IMPRINT",FACE,{"disambiguationData":[TD([[makeQuery(id+"F1.imprint","IMPRINT",EDGE,{"derivedFrom":subQ9}),-1.0]])]});}
            var Q3;
            {var subQ0=sQuery(id+"F1.wireOp",EDGE,"E17.left");var subQ1=sQuery(id+"F1.wireOp",EDGE,"E15");var subQ2=makeQuery(id+"F1.imprint","INTERSECT",VERTEX,{"disambiguationData":[OD(0.0)],"derivedFrom":[subQ1,subQ0]});Q3=makeQuery(id+"F1.imprint","IMPRINT",FACE,{"disambiguationData":[TD([[makeQuery(id+"F1.imprint","IMPRINT",EDGE,{"disambiguationData":[TD([[subQ2,1.0]])],"derivedFrom":subQ1}),1.0]])]});}
            var Q4;
            {var subQ1=sQuery(id+"F1.wireOp",EDGE,"E17.bottom");Q4=makeQuery(id+"F1.imprint","IMPRINT",FACE,{"disambiguationData":[TD([[makeQuery(id+"F1.imprint","IMPRINT",EDGE,{"derivedFrom":subQ1}),-1.0]])]});}
            var Q5;
            {var subQ6=sQuery(id+"F1.wireOp",EDGE,"E57");Q5=makeQuery(id+"F1.imprint","IMPRINT",FACE,{"disambiguationData":[TD([[makeQuery(id+"F1.imprint","IMPRINT",EDGE,{"derivedFrom":subQ6}),-1.0]])]});}
            var Q6;
            {var subQ0=sQuery(id+"F1.wireOp",EDGE,"E20.left");var subQ1=sQuery(id+"F1.wireOp",EDGE,"E18");var subQ2=makeQuery(id+"F1.imprint","INTERSECT",VERTEX,{"disambiguationData":[OD(0.0)],"derivedFrom":[subQ1,subQ0]});Q6=makeQuery(id+"F1.imprint","IMPRINT",FACE,{"disambiguationData":[TD([[makeQuery(id+"F1.imprint","IMPRINT",EDGE,{"disambiguationData":[TD([[subQ2,1.0]])],"derivedFrom":subQ1}),1.0]])]});}
            var Q7;
            {var subQ1=sQuery(id+"F1.wireOp",EDGE,"E20.bottom");Q7=makeQuery(id+"F1.imprint","IMPRINT",FACE,{"disambiguationData":[TD([[makeQuery(id+"F1.imprint","IMPRINT",EDGE,{"derivedFrom":subQ1}),-1.0]])]});}
            var Q8;
            {var subQ7=sQuery(id+"F1.wireOp",EDGE,"E22");Q8=makeQuery(id+"F1.imprint","IMPRINT",FACE,{"disambiguationData":[TD([[makeQuery(id+"F1.imprint","IMPRINT",EDGE,{"derivedFrom":subQ7}),-1.0]])]});}
            var Q9;
            {var subQ0=sQuery(id+"F1.wireOp",EDGE,"E25");Q9=makeQuery(id+"F1.imprint","IMPRINT",FACE,{"disambiguationData":[TD([[makeQuery(id+"F1.imprint","IMPRINT",EDGE,{"derivedFrom":subQ0}),1.0]])]});}
            var Q10;
            {var subQ0=sQuery(id+"F1.wireOp",EDGE,"iecyQkMB-DT64-ASyu-M7pA-KW5DgSD818Z4.left");var subQ1=sQuery(id+"F1.wireOp",EDGE,"E21");var subQ2=makeQuery(id+"F1.imprint","INTERSECT",VERTEX,{"disambiguationData":[OD(0.0)],"derivedFrom":[subQ1,subQ0]});Q10=makeQuery(id+"F1.imprint","IMPRINT",FACE,{"disambiguationData":[TD([[makeQuery(id+"F1.imprint","IMPRINT",EDGE,{"disambiguationData":[TD([[subQ2,1.0]])],"derivedFrom":subQ1}),1.0]])]});}
            var Q11;
            {var subQ3=sQuery(id+"F1.wireOp",EDGE,"E27.bottom");Q11=makeQuery(id+"F1.imprint","IMPRINT",FACE,{"disambiguationData":[TD([[makeQuery(id+"F1.imprint","IMPRINT",EDGE,{"derivedFrom":subQ3}),-1.0]])]});}
            var Q12;
            {var subQ1=sQuery(id+"F1.wireOp",EDGE,"E28");Q12=makeQuery(id+"F1.imprint","IMPRINT",FACE,{"disambiguationData":[TD([[makeQuery(id+"F1.imprint","IMPRINT",EDGE,{"derivedFrom":subQ1}),-1.0]])]});}
            var Q13;
            {var subQ5=sQuery(id+"F1.wireOp",EDGE,"E34.bottom");Q13=makeQuery(id+"F1.imprint","IMPRINT",FACE,{"disambiguationData":[TD([[makeQuery(id+"F1.imprint","IMPRINT",EDGE,{"derivedFrom":subQ5}),-1.0]])]});}
            var Q14;
            Q14=makeQuery(id+"F1.imprint","IMPRINT",FACE,{"disambiguationData":[TD([[makeQuery(id+"F1.imprint","IMPRINT",EDGE,{"derivedFrom":sQuery(id+"F1.wireOp",EDGE,"E35.bottom")}),-1.0]])]});
            var Q15;
            {var subQ3=sQuery(id+"F1.wireOp",EDGE,"E36.bottom");Q15=makeQuery(id+"F1.imprint","IMPRINT",FACE,{"disambiguationData":[TD([[makeQuery(id+"F1.imprint","IMPRINT",EDGE,{"derivedFrom":subQ3}),-1.0]])]});}
            var Q16;
            {var subQ1=sQuery(id+"F1.wireOp",EDGE,"E37.bottom");Q16=makeQuery(id+"F1.imprint","IMPRINT",FACE,{"disambiguationData":[TD([[makeQuery(id+"F1.imprint","IMPRINT",EDGE,{"derivedFrom":subQ1}),-1.0]])]});}
            var Q17;
            {var subQ1=sQuery(id+"F1.wireOp",EDGE,"E38");Q17=makeQuery(id+"F1.imprint","IMPRINT",FACE,{"disambiguationData":[TD([[makeQuery(id+"F1.imprint","IMPRINT",EDGE,{"derivedFrom":subQ1}),-1.0]])]});}
            var Q18;
            Q18=makeQuery(id+"F1.imprint","IMPRINT",FACE,{"disambiguationData":[TD([[makeQuery(id+"F1.imprint","IMPRINT",EDGE,{"derivedFrom":sQuery(id+"F1.wireOp",EDGE,"E44.bottom")}),-1.0]])]});
            var Q19;
            {var subQ0=sQuery(id+"F1.wireOp",EDGE,"E45");var subQ1=sQuery(id+"F1.wireOp",EDGE,"E42");var subQ2=makeQuery(id+"F1.imprint","INTERSECT",VERTEX,{"disambiguationData":[OD(0.0)],"derivedFrom":[subQ1,subQ0]});Q19=makeQuery(id+"F1.imprint","IMPRINT",FACE,{"disambiguationData":[TD([[makeQuery(id+"F1.imprint","IMPRINT",EDGE,{"disambiguationData":[TD([[subQ2,-1.0]])],"derivedFrom":subQ1}),1.0]])]});}
            var Q20;
            {var subQ3=sQuery(id+"F1.wireOp",EDGE,"E46");Q20=makeQuery(id+"F1.imprint","IMPRINT",FACE,{"disambiguationData":[TD([[makeQuery(id+"F1.imprint","IMPRINT",EDGE,{"derivedFrom":subQ3}),1.0]])]});}
            var Q21;
            {var subQ0=sQuery(id+"F1.wireOp",EDGE,"E67.left");var subQ1=sQuery(id+"F1.wireOp",EDGE,"E21");var subQ2=makeQuery(id+"F1.imprint","INTERSECT",VERTEX,{"disambiguationData":[OD(0.0)],"derivedFrom":[subQ1,subQ0]});Q21=makeQuery(id+"F1.imprint","IMPRINT",FACE,{"disambiguationData":[TD([[makeQuery(id+"F1.imprint","IMPRINT",EDGE,{"disambiguationData":[TD([[subQ2,1.0]])],"derivedFrom":subQ1}),1.0]])]});}
            var Q22;
            {var subQ1=sQuery(id+"F1.wireOp",EDGE,"E27.top");Q22=makeQuery(id+"F1.imprint","IMPRINT",FACE,{"disambiguationData":[TD([[makeQuery(id+"F1.imprint","IMPRINT",EDGE,{"derivedFrom":subQ1}),1.0]])]});}
            var Q23;
            Q23=makeQuery(id+"F4.opExtrude","CAP_FACE",FACE,{"disambiguationData":[OSD([sQuery(id+"F3.wireOp",EDGE,"E80.top"),sQuery(id+"F3.wireOp",EDGE,"E80.left"),sQuery(id+"F3.wireOp",EDGE,"E80.right"),sQuery(id+"F3.wireOp",EDGE,"E82.left"),sQuery(id+"F3.wireOp",EDGE,"E82.right"),sQuery(id+"F3.wireOp",EDGE,"E83.bottom"),sQuery(id+"F3.wireOp",EDGE,"E83.top"),sQuery(id+"F3.wireOp",EDGE,"E83.right"),sQuery(id+"F3.wireOp",EDGE,"E84.top"),sQuery(id+"F3.wireOp",EDGE,"E84.right"),sQuery(id+"F3.wireOp",EDGE,"E85.bottom"),sQuery(id+"F3.wireOp",EDGE,"E85.top"),sQuery(id+"F3.wireOp",EDGE,"E85.right"),sQuery(id+"F3.wireOp",EDGE,"E88"),sQuery(id+"F3.wireOp",EDGE,"E89"),sQuery(id+"F3.wireOp",EDGE,"E90"),sQuery(id+"F3.wireOp",EDGE,"E91"),sQuery(id+"F3.wireOp",EDGE,"E94"),sQuery(id+"F3.wireOp",EDGE,"E95"),sQuery(id+"F3.wireOp",EDGE,"E96"),sQuery(id+"F3.wireOp",EDGE,"E97"),sQuery(id+"F3.wireOp",EDGE,"E98")])],"isStart":false});
            extrude(context, id + "F5", {"entities" : qUnion([Q0, Q1, Q2, Q3, Q4, Q5, Q6, Q7, Q8, Q9, Q10, Q11, Q12, Q13, Q14, Q15, Q16, Q17, Q18, Q19, Q20, Q21, Q22, Q23]), "operationType" : NewBodyOperationType.ADD, "depth" : 100 * mm, "offsetDistance" : 25 * mm});
        }
        {
            var Q0;
            Q0=makeQuery(id+"F0.imprint","IMPRINT",FACE,{"disambiguationData":[TD([[makeQuery(id+"F0.imprint","IMPRINT",EDGE,{"derivedFrom":sQuery(id+"F0.wireOp",EDGE,"E2.bottom")}),-1.0]])]});
            var Q1;
            {var subQ0=sQuery(id+"F0.wireOp",EDGE,"E0.bottom");Q1=makeQuery(id+"F0.imprint","IMPRINT",FACE,{"disambiguationData":[TD([[makeQuery(id+"F0.imprint","IMPRINT",EDGE,{"derivedFrom":subQ0}),-1.0]])]});}
            var Q2;
            Q2=makeQuery(id+"F0.imprint","IMPRINT",FACE,{"disambiguationData":[TD([[makeQuery(id+"F0.imprint","IMPRINT",EDGE,{"derivedFrom":sQuery(id+"F0.wireOp",EDGE,"E1.bottom")}),-1.0]])]});
            var Q3;
            {var subQ4=sQuery(id+"F0.wireOp",EDGE,"E3.bottom");Q3=makeQuery(id+"F0.imprint","IMPRINT",FACE,{"disambiguationData":[TD([[makeQuery(id+"F0.imprint","IMPRINT",EDGE,{"derivedFrom":subQ4}),-1.0]])]});}
            var Q4;
            {var subQ0=sQuery(id+"F0.wireOp",EDGE,"E5.bottom");Q4=makeQuery(id+"F0.imprint","IMPRINT",FACE,{"disambiguationData":[TD([[makeQuery(id+"F0.imprint","IMPRINT",EDGE,{"derivedFrom":subQ0}),1.0]])]});}
            var Q5;
            Q5=makeQuery(id+"F0.imprint","IMPRINT",FACE,{"disambiguationData":[TD([[makeQuery(id+"F0.imprint","IMPRINT",EDGE,{"derivedFrom":sQuery(id+"F0.wireOp",EDGE,"E6.bottom")}),1.0]])]});
            var Q6;
            {var subQ0=sQuery(id+"F0.wireOp",EDGE,"E4.bottom");Q6=makeQuery(id+"F0.imprint","IMPRINT",FACE,{"disambiguationData":[TD([[makeQuery(id+"F0.imprint","IMPRINT",EDGE,{"derivedFrom":subQ0}),-1.0]])]});}
            var Q7;
            {var subQ3=sQuery(id+"F0.wireOp",EDGE,"E7.bottom");Q7=makeQuery(id+"F0.imprint","IMPRINT",FACE,{"disambiguationData":[TD([[makeQuery(id+"F0.imprint","IMPRINT",EDGE,{"derivedFrom":subQ3}),-1.0]])]});}
            var Q8;
            {var subQ1=sQuery(id+"F0.wireOp",EDGE,"E9");Q8=makeQuery(id+"F0.imprint","IMPRINT",FACE,{"disambiguationData":[TD([[makeQuery(id+"F0.imprint","IMPRINT",EDGE,{"derivedFrom":subQ1}),-1.0]])]});}
            var Q9;
            {var subQ3=sQuery(id+"F0.wireOp",EDGE,"E8.bottom");Q9=makeQuery(id+"F0.imprint","IMPRINT",FACE,{"disambiguationData":[TD([[makeQuery(id+"F0.imprint","IMPRINT",EDGE,{"derivedFrom":subQ3}),-1.0]])]});}
            var Q10;
            {var subQ0=sQuery(id+"F1.wireOp",EDGE,"E27.left");Q10=makeQuery(id+"F1.imprint","IMPRINT",FACE,{"disambiguationData":[TD([[makeQuery(id+"F1.imprint","IMPRINT",EDGE,{"derivedFrom":subQ0}),-1.0]])]});}
            var Q11;
            {var subQ0=sQuery(id+"F1.wireOp",EDGE,"E67.left");var subQ1=sQuery(id+"F1.wireOp",EDGE,"E60");var subQ2=makeQuery(id+"F1.imprint","INTERSECT",VERTEX,{"derivedFrom":[subQ1,subQ0]});Q11=makeQuery(id+"F1.imprint","IMPRINT",FACE,{"disambiguationData":[TD([[makeQuery(id+"F1.imprint","IMPRINT",EDGE,{"disambiguationData":[TD([[subQ2,-1.0]])],"derivedFrom":subQ1}),-1.0]])]});}
            var Q12;
            {var subQ14=sQuery(id+"F1.wireOp",EDGE,"E67.bottom");Q12=makeQuery(id+"F1.imprint","IMPRINT",FACE,{"disambiguationData":[TD([[makeQuery(id+"F1.imprint","IMPRINT",EDGE,{"derivedFrom":subQ14}),-1.0]])]});}
            extrude(context, id + "F6", {"entities" : qUnion([Q0, Q1, Q2, Q3, Q4, Q5, Q6, Q7, Q8, Q9, Q10, Q11, Q12]), "operationType" : NewBodyOperationType.ADD, "depth" : 100 * mm, "offsetDistance" : 25 * mm});
        }
        {
            var Q0;
            {var subQ0=sQuery(id+"F1.wireOp",EDGE,"E67.left");var subQ1=sQuery(id+"F1.wireOp",EDGE,"E67.top");var subQ2=sQuery(id+"F1.wireOp",EDGE,"E27.left");var subQ3=sQuery(id+"F1.wireOp",EDGE,"E27.bottom");var subQ4=sQuery(id+"F1.wireOp",EDGE,"E21");Q0=makeQuery(id+"F6.boolean.opBoolean","MERGE",FACE,{"derivedFrom":[makeQuery(id+"F5.boolean.opBoolean","MERGE",FACE,{"derivedFrom":[makeQuery(id+"F4.opExtrude","CAP_FACE",FACE,{"disambiguationData":[OSD([sQuery(id+"F3.wireOp",EDGE,"l2BAxcx8-wpF1-YFFp-7Sex-uG9L4fK84GIy"),sQuery(id+"F3.wireOp",EDGE,"E80.bottom"),sQuery(id+"F3.wireOp",EDGE,"E80.top"),sQuery(id+"F3.wireOp",EDGE,"E80.left"),sQuery(id+"F3.wireOp",EDGE,"E80.right"),sQuery(id+"F3.wireOp",EDGE,"QoJ9POKL-7dSj-Kbwg-M42Z-KDTpscI53ORy"),sQuery(id+"F3.wireOp",EDGE,"5uwGIrsL-Ax3l-KrJ3-TsMS-mPTyOWhAeuEh"),sQuery(id+"F3.wireOp",EDGE,"E82.left"),sQuery(id+"F3.wireOp",EDGE,"E82.right"),sQuery(id+"F3.wireOp",EDGE,"E83.bottom"),sQuery(id+"F3.wireOp",EDGE,"E83.top"),sQuery(id+"F3.wireOp",EDGE,"E83.right"),sQuery(id+"F3.wireOp",EDGE,"E84.top"),sQuery(id+"F3.wireOp",EDGE,"E84.right"),sQuery(id+"F3.wireOp",EDGE,"E85.bottom"),sQuery(id+"F3.wireOp",EDGE,"E85.top"),sQuery(id+"F3.wireOp",EDGE,"E85.right"),sQuery(id+"F3.wireOp",EDGE,"E88"),sQuery(id+"F3.wireOp",EDGE,"E89"),sQuery(id+"F3.wireOp",EDGE,"E90"),sQuery(id+"F3.wireOp",EDGE,"etVh0nDV-C5XI-KxPU-PWaB-zNqrgVtYXJuy"),sQuery(id+"F3.wireOp",EDGE,"9Uwg85qv-AG06-xsUL-vuyy-mQr5ySh0xjGx"),sQuery(id+"F3.wireOp",EDGE,"GElmIXpN-kcJR-45oa-h3sK-QHrJCuWuAJcQ"),sQuery(id+"F3.wireOp",EDGE,"goEZywdV-8XkG-8Sym-g4On-3OGV7yo023wS"),sQuery(id+"F3.wireOp",EDGE,"vgvU5bvX-y910-j5x7-Pnl7-edi9nkagyyvk"),sQuery(id+"F3.wireOp",EDGE,"A0sOWVF3-NyLm-6ixX-yWYj-byc4YMwfl8ZQ"),sQuery(id+"F3.wireOp",EDGE,"6rbocMI0-TDBY-w5Uv-wJxH-Qzmedno7K920"),sQuery(id+"F3.wireOp",EDGE,"bWhbsvP7-AFgO-Zpik-0wAH-UOQKSabqtz7W"),sQuery(id+"F3.wireOp",EDGE,"950Jbx4t-1ap7-0Oa0-OCDV-OI8zhHYVOVjz"),sQuery(id+"F3.wireOp",EDGE,"DhwoowST-LI71-TCD9-Jlqx-Kfxn5UWzSTiA"),sQuery(id+"F3.wireOp",EDGE,"E93"),sQuery(id+"F3.wireOp",EDGE,"Tai5gYko-rnaj-8Qc9-2tER-s00ccv3sg9T1"),sQuery(id+"F3.wireOp",EDGE,"5q8jDOtX-27Ef-KL8C-5kjW-WqSuiysjhouQ"),sQuery(id+"F3.wireOp",EDGE,"JoOKKDIO-IGdM-3Qr5-9c63-hFw5rqBlnuZK"),sQuery(id+"F3.wireOp",EDGE,"UGmMbKpx-ic0C-BP45-GIFm-G44WuJZ7rcJZ"),sQuery(id+"F3.wireOp",EDGE,"ZULs1xFT-bYxo-X5Mw-NcRk-gdkzuhtu9iQL")])],"isStart":false}),makeQuery(id+"F5.opExtrude","CAP_FACE",FACE,{"disambiguationData":[OSD([sQuery(id+"F1.wireOp",EDGE,"E14.bottom"),sQuery(id+"F1.wireOp",EDGE,"E14.top"),sQuery(id+"F1.wireOp",EDGE,"E14.left"),sQuery(id+"F1.wireOp",EDGE,"E15"),sQuery(id+"F1.wireOp",EDGE,"E16"),sQuery(id+"F1.wireOp",EDGE,"E17.bottom"),sQuery(id+"F1.wireOp",EDGE,"E17.top"),sQuery(id+"F1.wireOp",EDGE,"E17.left"),sQuery(id+"F1.wireOp",EDGE,"E17.right"),sQuery(id+"F1.wireOp",EDGE,"E18"),sQuery(id+"F1.wireOp",EDGE,"E20.bottom"),sQuery(id+"F1.wireOp",EDGE,"E20.top"),sQuery(id+"F1.wireOp",EDGE,"E20.left"),sQuery(id+"F1.wireOp",EDGE,"E20.right"),subQ4,sQuery(id+"F1.wireOp",EDGE,"E22"),sQuery(id+"F1.wireOp",EDGE,"E25"),sQuery(id+"F1.wireOp",EDGE,"E56"),sQuery(id+"F1.wireOp",EDGE,"E57"),sQuery(id+"F1.wireOp",EDGE,"E58"),sQuery(id+"F1.wireOp",EDGE,"E60"),sQuery(id+"F1.wireOp",EDGE,"E66"),subQ1,subQ0])],"isStart":false}),makeQuery(id+"F5.opExtrude","CAP_FACE",FACE,{"disambiguationData":[OSD([subQ3,sQuery(id+"F1.wireOp",EDGE,"E27.top"),subQ2,sQuery(id+"F1.wireOp",EDGE,"E27.right"),sQuery(id+"F1.wireOp",EDGE,"E28"),sQuery(id+"F1.wireOp",EDGE,"E29"),sQuery(id+"F1.wireOp",EDGE,"E30"),sQuery(id+"F1.wireOp",EDGE,"E31"),sQuery(id+"F1.wireOp",EDGE,"E32"),sQuery(id+"F1.wireOp",EDGE,"E33"),sQuery(id+"F1.wireOp",EDGE,"E34.bottom"),sQuery(id+"F1.wireOp",EDGE,"E34.top"),sQuery(id+"F1.wireOp",EDGE,"E35.top"),sQuery(id+"F1.wireOp",EDGE,"E35.left"),sQuery(id+"F1.wireOp",EDGE,"E35.right"),sQuery(id+"F1.wireOp",EDGE,"E36.bottom"),sQuery(id+"F1.wireOp",EDGE,"E36.top"),sQuery(id+"F1.wireOp",EDGE,"E36.left"),sQuery(id+"F1.wireOp",EDGE,"E36.right"),sQuery(id+"F1.wireOp",EDGE,"E37.bottom"),sQuery(id+"F1.wireOp",EDGE,"E37.top"),sQuery(id+"F1.wireOp",EDGE,"E37.right"),sQuery(id+"F1.wireOp",EDGE,"E38"),sQuery(id+"F1.wireOp",EDGE,"E39"),sQuery(id+"F1.wireOp",EDGE,"E40"),sQuery(id+"F1.wireOp",EDGE,"E41"),sQuery(id+"F1.wireOp",EDGE,"E42"),sQuery(id+"F1.wireOp",EDGE,"E43"),sQuery(id+"F1.wireOp",EDGE,"E44.bottom"),sQuery(id+"F1.wireOp",EDGE,"E44.top"),sQuery(id+"F1.wireOp",EDGE,"E44.left"),sQuery(id+"F1.wireOp",EDGE,"E44.right"),sQuery(id+"F1.wireOp",EDGE,"E45"),sQuery(id+"F1.wireOp",EDGE,"E46"),sQuery(id+"F1.wireOp",EDGE,"E47"),sQuery(id+"F1.wireOp",EDGE,"E48"),sQuery(id+"F1.wireOp",EDGE,"E50"),sQuery(id+"F1.wireOp",EDGE,"E51"),subQ1])],"isStart":false}),makeQuery(id+"F5.opExtrude","CAP_FACE",FACE,{"disambiguationData":[OSD([sQuery(id+"F2.wireOp",EDGE,"E70"),sQuery(id+"F2.wireOp",EDGE,"E71"),sQuery(id+"F2.wireOp",EDGE,"E72"),sQuery(id+"F2.wireOp",EDGE,"E73"),sQuery(id+"F2.wireOp",EDGE,"E74"),sQuery(id+"F2.wireOp",EDGE,"E75"),sQuery(id+"F2.wireOp",EDGE,"E76"),sQuery(id+"F2.wireOp",EDGE,"E77"),sQuery(id+"F2.wireOp",EDGE,"E78")])],"isStart":false})]}),makeQuery(id+"F6.opExtrude","CAP_FACE",FACE,{"disambiguationData":[OSD([sQuery(id+"F0.wireOp",EDGE,"E0.bottom"),sQuery(id+"F0.wireOp",EDGE,"E0.top"),sQuery(id+"F0.wireOp",EDGE,"E0.left"),sQuery(id+"F0.wireOp",EDGE,"E1.bottom"),sQuery(id+"F0.wireOp",EDGE,"E1.top"),sQuery(id+"F0.wireOp",EDGE,"E1.left"),sQuery(id+"F0.wireOp",EDGE,"E2.left"),sQuery(id+"F0.wireOp",EDGE,"E3.bottom"),sQuery(id+"F0.wireOp",EDGE,"E3.top"),sQuery(id+"F0.wireOp",EDGE,"E3.right"),sQuery(id+"F0.wireOp",EDGE,"E4.bottom"),sQuery(id+"F0.wireOp",EDGE,"E4.top"),sQuery(id+"F0.wireOp",EDGE,"E5.bottom"),sQuery(id+"F0.wireOp",EDGE,"E5.top"),sQuery(id+"F0.wireOp",EDGE,"E6.bottom"),sQuery(id+"F0.wireOp",EDGE,"E6.top"),sQuery(id+"F0.wireOp",EDGE,"E6.right"),sQuery(id+"F0.wireOp",EDGE,"E7.bottom"),sQuery(id+"F0.wireOp",EDGE,"E7.top"),sQuery(id+"F0.wireOp",EDGE,"E7.left"),sQuery(id+"F0.wireOp",EDGE,"E7.right"),sQuery(id+"F0.wireOp",EDGE,"E8.bottom"),sQuery(id+"F0.wireOp",EDGE,"E8.top"),sQuery(id+"F0.wireOp",EDGE,"E8.left"),sQuery(id+"F0.wireOp",EDGE,"E8.right"),sQuery(id+"F0.wireOp",EDGE,"E9"),sQuery(id+"F0.wireOp",EDGE,"E10"),sQuery(id+"F0.wireOp",EDGE,"E11"),sQuery(id+"F0.wireOp",EDGE,"E12"),sQuery(id+"F0.wireOp",EDGE,"E13.bottom"),sQuery(id+"F0.wireOp",EDGE,"E13.top"),sQuery(id+"F0.wireOp",EDGE,"E2.right"),sQuery(id+"F0.wireOp",EDGE,"E13.right")])],"isStart":false}),makeQuery(id+"F6.opExtrude","CAP_FACE",FACE,{"disambiguationData":[OSD([subQ4,subQ3,subQ2,sQuery(id+"F1.wireOp",EDGE,"E67.bottom"),subQ1,subQ0,sQuery(id+"F1.wireOp",EDGE,"E67.right")])],"isStart":false})]});}
            var sketch = newSketch(context, id + "F7", { "sketchPlane" : qUnion([Q0])});
            skLineSegment(sketch, "E104.bottom", {"start": v(-52.42, 70.35) * mm, "end": v(-44.12, 70.35) * mm});
            skLineSegment(sketch, "E104.top", {"start": v(-52.42, -14.63) * mm, "end": v(-44.12, -14.63) * mm});
            skLineSegment(sketch, "E104.left", {"start": v(-52.42, 70.35) * mm, "end": v(-52.42, -14.63) * mm});
            skLineSegment(sketch, "E104.right", {"start": v(-44.12, 70.35) * mm, "end": v(-44.12, -14.63) * mm});
            skLineSegment(sketch, "E105.bottom", {"start": v(-16.76, 70.35) * mm, "end": v(-8.46, 70.35) * mm});
            skLineSegment(sketch, "E105.top", {"start": v(-16.76, -14.63) * mm, "end": v(-8.46, -14.63) * mm});
            skLineSegment(sketch, "E105.left", {"start": v(-16.76, 70.35) * mm, "end": v(-16.76, -14.63) * mm});
            skLineSegment(sketch, "E105.right", {"start": v(-8.46, 70.35) * mm, "end": v(-8.46, -14.63) * mm});
            skLineSegment(sketch, "E106.bottom", {"start": v(-26.81, -14.63) * mm, "end": v(-25.2, -14.63) * mm});
            skLineSegment(sketch, "E106.top", {"start": v(-26.81, -39.15) * mm, "end": v(-25.2, -39.15) * mm});
            skLineSegment(sketch, "E106.left", {"start": v(-26.81, -14.63) * mm, "end": v(-26.81, -39.15) * mm});
            skLineSegment(sketch, "E106.right", {"start": v(-25.2, -14.63) * mm, "end": v(-25.2, -39.15) * mm});
            skLineSegment(sketch, "E107.bottom", {"start": v(13.52, -14.77) * mm, "end": v(15.3, -14.77) * mm});
            skLineSegment(sketch, "E107.top", {"start": v(13.52, -26.89) * mm, "end": v(15.3, -26.89) * mm});
            skLineSegment(sketch, "E107.left", {"start": v(13.52, -14.77) * mm, "end": v(13.52, -26.89) * mm});
            skLineSegment(sketch, "E107.right", {"start": v(15.3, -14.77) * mm, "end": v(15.3, -26.89) * mm});
            skLineSegment(sketch, "E108.bottom", {"start": v(6.75, -14.77) * mm, "end": v(7.49, -14.77) * mm});
            skLineSegment(sketch, "E108.top", {"start": v(6.75, -19.85) * mm, "end": v(7.49, -19.85) * mm});
            skLineSegment(sketch, "E108.left", {"start": v(6.75, -14.77) * mm, "end": v(6.75, -19.85) * mm});
            skLineSegment(sketch, "E108.right", {"start": v(7.49, -14.77) * mm, "end": v(7.49, -19.85) * mm});
            skLineSegment(sketch, "E109.bottom", {"start": v(-7.11, -14.77) * mm, "end": v(-6.1, -14.77) * mm});
            skLineSegment(sketch, "E109.top", {"start": v(-7.11, -19.85) * mm, "end": v(-6.1, -19.85) * mm});
            skLineSegment(sketch, "E109.left", {"start": v(-7.11, -14.77) * mm, "end": v(-7.11, -19.85) * mm});
            skLineSegment(sketch, "E109.right", {"start": v(-6.1, -14.77) * mm, "end": v(-6.1, -19.85) * mm});
            skLineSegment(sketch, "E110.bottom", {"start": v(42.34, 70.35) * mm, "end": v(53.6, 70.35) * mm});
            skLineSegment(sketch, "E110.top", {"start": v(42.34, -14.63) * mm, "end": v(53.6, -14.63) * mm});
            skLineSegment(sketch, "E110.left", {"start": v(42.34, 70.35) * mm, "end": v(42.34, -14.63) * mm});
            skLineSegment(sketch, "E110.right", {"start": v(53.6, 70.35) * mm, "end": v(53.6, -14.63) * mm});
            skSolve(sketch);
        }
        {
            var Q0;
            Q0 = qSketchRegion(id + "F7", true);
            extrude(context, id + "F8", {"entities" : qUnion([Q0]), "operationType" : NewBodyOperationType.REMOVE, "oppositeDirection" : true, "depth" : 70 * mm, "offsetDistance" : 25 * mm});
        }
        {
            var Q0;
            Q0=makeQuery(id+"F5.opExtrude","SWEPT_FACE",FACE,{"disambiguationData":[OSD([sQuery(id+"F1.wireOp",EDGE,"E44.right")])]});
            var sketch = newSketch(context, id + "F9", { "sketchPlane" : qUnion([Q0])});
            skLineSegment(sketch, "E111", {"start": v(112.33, 120.02) * mm, "end": v(-139.1, 0) * mm});
            skLineSegment(sketch, "E112", {"start": v(-151.65, 117.38) * mm, "end": v(-139.1, 0) * mm});
            skLineSegment(sketch, "E113", {"start": v(112.33, 120.02) * mm, "end": v(111.15, 237.74) * mm});
            skLineSegment(sketch, "E114", {"start": v(-151.65, 117.38) * mm, "end": v(-152.93, 246) * mm});
            skLineSegment(sketch, "E115", {"start": v(111.15, 237.74) * mm, "end": v(-152.93, 246) * mm});
            skSolve(sketch);
        }
        {
            var Q0;
            Q0 = qSketchRegion(id + "F9", true);
            extrude(context, id + "F10", {"entities" : qUnion([Q0]), "operationType" : NewBodyOperationType.REMOVE, "oppositeDirection" : true, "depth" : 200 * mm, "offsetDistance" : 25 * mm});
        }
    });
